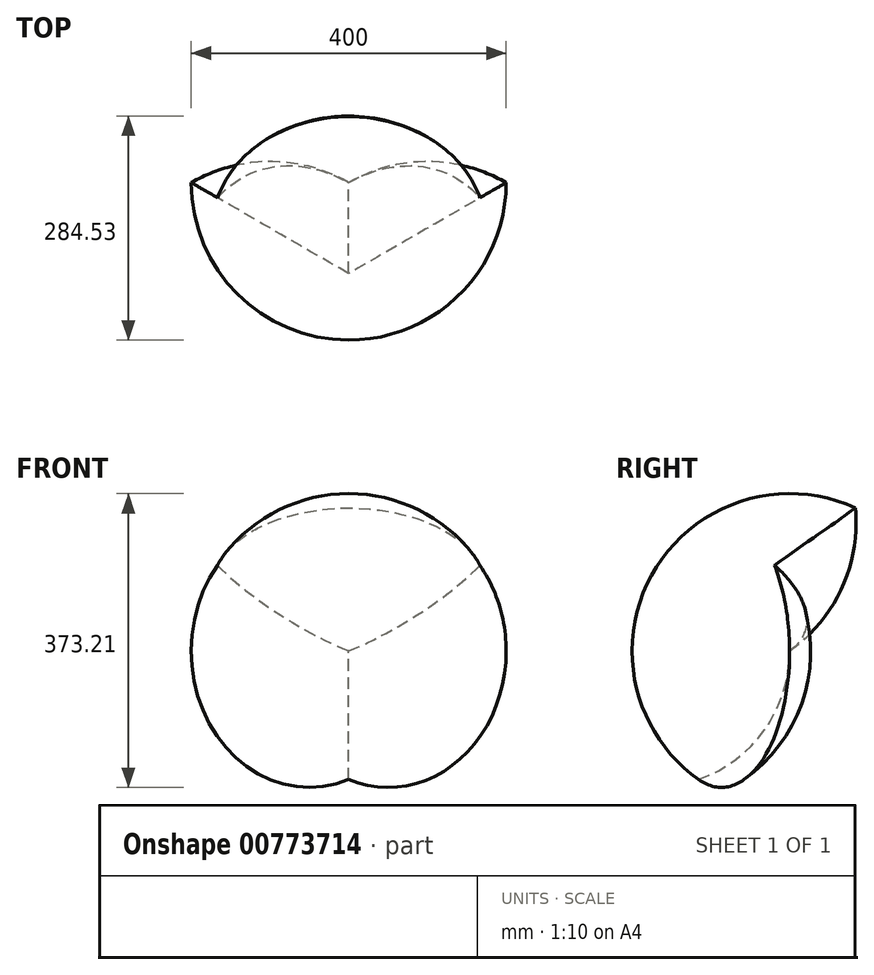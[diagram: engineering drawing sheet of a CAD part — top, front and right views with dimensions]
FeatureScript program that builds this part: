
annotation { "Feature Type Name" : "Feature", "Feature Type Description" : "" }
export const myFeature = defineFeature(function(context is Context, id is Id, definition is map)
    precondition{}
    {
        {
            var Q0;
            Q0=qCreatedBy(makeId("Top.planeOp"),FACE);
            var sketch = newSketch(context, id + "F0", { "sketchPlane" : qUnion([Q0])});
            skLineSegment(sketch, "E0", {"start": v(0, 115.47) * mm, "end": v(100, -57.74) * mm});
            skLineSegment(sketch, "E1", {"start": v(100, -57.74) * mm, "end": v(-100, -57.74) * mm});
            skLineSegment(sketch, "E2", {"start": v(-100, -57.74) * mm, "end": v(0, 115.47) * mm});
            skLineSegment(sketch, "E3", {"start": v(0, 115.47) * mm, "end": v(0, 0) * mm});
            skLineSegment(sketch, "E4", {"start": v(-100, -57.74) * mm, "end": v(0, 0) * mm});
            skLineSegment(sketch, "E5", {"start": v(0, 0) * mm, "end": v(100, -57.74) * mm});
            skPoint(sketch, "E6.orphan", {"position": v(0, -57.74) * mm});
            skLineSegment(sketch, "E7", {"start": v(0, 115.47) * mm, "end": v(0, -57.74) * mm, "construction": true});
            skCircle(sketch, "E8", {"center": v(0, 115.47) * mm, "radius": 200 * mm});
            skCircle(sketch, "E9", {"center": v(-100, -57.74) * mm, "radius": 200 * mm});
            skCircle(sketch, "E10", {"center": v(100, -57.74) * mm, "radius": 200 * mm});
            skLineSegment(sketch, "E11", {"start": v(-50, 28.87) * mm, "end": v(100, -57.74) * mm});
            skLineSegment(sketch, "E12", {"start": v(0, 115.47) * mm, "end": v(0, -57.74) * mm});
            skLineSegment(sketch, "E13", {"start": v(0, 115.47) * mm, "end": v(0, -84.53) * mm});
            skLineSegment(sketch, "E14", {"start": v(0, -84.53) * mm, "end": v(0, 315.47) * mm});
            skLineSegment(sketch, "E15", {"start": v(0, 315.47) * mm, "end": v(0, 115.47) * mm});
            skLineSegment(sketch, "E16", {"start": v(100, -57.74) * mm, "end": v(273.2, -157.74) * mm});
            skLineSegment(sketch, "E17", {"start": v(273.2, -157.74) * mm, "end": v(-73.2, 42.26) * mm});
            skLineSegment(sketch, "E18", {"start": v(-73.2, 42.26) * mm, "end": v(100, -57.74) * mm});
            skLineSegment(sketch, "E19", {"start": v(0, 0) * mm, "end": v(-273.2, -157.74) * mm});
            skLineSegment(sketch, "E20", {"start": v(-273.2, -157.74) * mm, "end": v(73.2, 42.26) * mm});
            skLineSegment(sketch, "E21", {"start": v(73.2, 42.26) * mm, "end": v(0, 0) * mm});
            skSolve(sketch);
        }
        {
            assignVariable(context, id + "F1", {"name" : "Angle", "anyValue" : 70.53});
        }
        {
            var Q0;
            {var subQ1=sQuery(id+"F0.wireOp",EDGE,"E3");var subQ6=sQuery(id+"F0.wireOp",EDGE,"E4");Q0=qUnion([makeQuery(id+"F0.imprint","IMPRINT",FACE,{"disambiguationData":[TD([[makeQuery(id+"F0.imprint","IMPRINT",EDGE,{"derivedFrom":subQ6}),1.0]])]}),makeQuery(id+"F0.imprint","IMPRINT",FACE,{"disambiguationData":[TD([[makeQuery(id+"F0.imprint","IMPRINT",EDGE,{"derivedFrom":subQ1}),-1.0]])]})]);}
            var Q1;
            {var subQ1=sQuery(id+"F0.wireOp",EDGE,"E5");var subQ5=sQuery(id+"F0.wireOp",EDGE,"E3");Q1=qUnion([makeQuery(id+"F0.imprint","IMPRINT",FACE,{"disambiguationData":[TD([[makeQuery(id+"F0.imprint","IMPRINT",EDGE,{"derivedFrom":subQ5}),1.0]])]}),makeQuery(id+"F0.imprint","IMPRINT",FACE,{"disambiguationData":[TD([[makeQuery(id+"F0.imprint","IMPRINT",EDGE,{"derivedFrom":subQ1}),1.0]])]})]);}
            var Q2;
            {var subQ1=sQuery(id+"F0.wireOp",EDGE,"E5");var subQ6=sQuery(id+"F0.wireOp",EDGE,"E4");Q2=qUnion([makeQuery(id+"F0.imprint","IMPRINT",FACE,{"disambiguationData":[TD([[makeQuery(id+"F0.imprint","IMPRINT",EDGE,{"derivedFrom":subQ6}),-1.0]])]}),makeQuery(id+"F0.imprint","IMPRINT",FACE,{"disambiguationData":[TD([[makeQuery(id+"F0.imprint","IMPRINT",EDGE,{"derivedFrom":subQ1}),-1.0]])]})]);}
            extrude(context, id + "F2", {"entities" : qUnion([Q0, Q1, Q2]), "depth" : 1000 * mm, "hasDraft" : true, "draftAngle" : (90 - getVariable(context, 'Angle')) * degree, "draftPullDirection" : true, "offsetDistance" : 25 * mm});
        }
        {
            var Q0;
            Q0=qCreatedBy(makeId("Top.planeOp"),FACE);
            cPlane(context, id + "F3", {"entities" : qUnion([Q0]), "cplaneType" : CPlaneType.OFFSET, "offset" : 163.3 * mm, "width" : 150 * mm, "height" : 150 * mm});
        }
        {
            var Q0;
            Q0=qCreatedBy(id+"F3.planeOp",FACE);
            var sketch = newSketch(context, id + "F4", { "sketchPlane" : qUnion([Q0])});
            skCircle(sketch, "E22", {"center": v(0, 0) * mm, "radius": 200 * mm});
            skLineSegment(sketch, "E23", {"start": v(0, 0) * mm, "end": v(0, 200) * mm});
            skLineSegment(sketch, "E24", {"start": v(0, 200) * mm, "end": v(0, -200) * mm});
            skLineSegment(sketch, "E25", {"start": v(0, -200) * mm, "end": v(0, 0) * mm});
            skSolve(sketch);
        }
        {
            var Q0;
            {var subQ0=sQuery(id+"F4.wireOp",EDGE,"E24");Q0=makeQuery(id+"F4.imprint","IMPRINT",FACE,{"disambiguationData":[TD([[makeQuery(id+"F4.imprint","IMPRINT",EDGE,{"derivedFrom":subQ0}),1.0]])]});}
            var Q1;
            Q1=sQuery(id+"F4.wireOp",EDGE,"E24");
            revolve(context, id + "F5", {"surfaceOperationType" : NewSurfaceOperationType.NEW, "entities" : qUnion([Q0]), "axis" : qUnion([Q1]), "revolveType" : RevolveType.FULL});
        }
        {
            var Q0;
            {var subQ0=sQuery(id+"F0.wireOp",EDGE,"E19");Q0=makeQuery(id+"F0.imprint","IMPRINT",FACE,{"disambiguationData":[TD([[makeQuery(id+"F0.imprint","IMPRINT",EDGE,{"derivedFrom":subQ0}),1.0]])]});}
            var Q1;
            {var subQ1=sQuery(id+"F0.wireOp",EDGE,"E8");var subQ4=makeQuery(id+"F0.imprint","INTERSECT",VERTEX,{"derivedFrom":[subQ1,sQuery(id+"F0.wireOp",EDGE,"E13")]});Q1=makeQuery(id+"F0.imprint","IMPRINT",FACE,{"disambiguationData":[TD([[makeQuery(id+"F0.imprint","IMPRINT",EDGE,{"disambiguationData":[TD([[subQ4,1.0]])],"derivedFrom":subQ1}),-1.0]])]});}
            var Q2;
            {var subQ3=sQuery(id+"F0.wireOp",EDGE,"E13");Q2=makeQuery(id+"F0.imprint","IMPRINT",FACE,{"disambiguationData":[TD([[makeQuery(id+"F0.imprint","IMPRINT",EDGE,{"derivedFrom":subQ3}),1.0]])]});}
            var Q3;
            {var subQ0=sQuery(id+"F0.wireOp",EDGE,"E13");Q3=makeQuery(id+"F0.imprint","IMPRINT",FACE,{"disambiguationData":[TD([[makeQuery(id+"F0.imprint","IMPRINT",EDGE,{"derivedFrom":subQ0}),-1.0]])]});}
            var Q4;
            {var subQ2=sQuery(id+"F0.wireOp",EDGE,"E4");Q4=makeQuery(id+"F0.imprint","IMPRINT",FACE,{"disambiguationData":[TD([[makeQuery(id+"F0.imprint","IMPRINT",EDGE,{"derivedFrom":subQ2}),-1.0]])]});}
            var Q5;
            {var subQ0=sQuery(id+"F0.wireOp",EDGE,"E5");Q5=makeQuery(id+"F0.imprint","IMPRINT",FACE,{"disambiguationData":[TD([[makeQuery(id+"F0.imprint","IMPRINT",EDGE,{"derivedFrom":subQ0}),-1.0]])]});}
            var Q6;
            {var subQ0=sQuery(id+"F0.wireOp",EDGE,"E9");var subQ3=sQuery(id+"F0.wireOp",EDGE,"E20");var subQ5=makeQuery(id+"F0.imprint","INTERSECT",VERTEX,{"derivedFrom":[subQ0,subQ3]});Q6=makeQuery(id+"F0.imprint","IMPRINT",FACE,{"disambiguationData":[TD([[makeQuery(id+"F0.imprint","IMPRINT",EDGE,{"disambiguationData":[TD([[subQ5,1.0]])],"derivedFrom":subQ3}),-1.0]])]});}
            var Q7;
            {var subQ0=sQuery(id+"F0.wireOp",EDGE,"E5");Q7=makeQuery(id+"F0.imprint","IMPRINT",FACE,{"disambiguationData":[TD([[makeQuery(id+"F0.imprint","IMPRINT",EDGE,{"derivedFrom":subQ0}),1.0]])]});}
            var Q8;
            Q8=sQuery(id+"F0.wireOp",EDGE,"E19");
            revolve(context, id + "F6", {"surfaceOperationType" : NewSurfaceOperationType.NEW, "entities" : qUnion([Q0, Q1, Q2, Q3, Q4, Q5, Q6, Q7]), "axis" : qUnion([Q8]), "revolveType" : RevolveType.FULL});
        }
        {
            var Q0;
            {var subQ0=sQuery(id+"F0.wireOp",EDGE,"E16");Q0=makeQuery(id+"F0.imprint","IMPRINT",FACE,{"disambiguationData":[TD([[makeQuery(id+"F0.imprint","IMPRINT",EDGE,{"derivedFrom":subQ0}),-1.0]])]});}
            var Q1;
            {var subQ1=sQuery(id+"F0.wireOp",EDGE,"E8");var subQ4=makeQuery(id+"F0.imprint","INTERSECT",VERTEX,{"derivedFrom":[subQ1,sQuery(id+"F0.wireOp",EDGE,"E13")]});Q1=makeQuery(id+"F0.imprint","IMPRINT",FACE,{"disambiguationData":[TD([[makeQuery(id+"F0.imprint","IMPRINT",EDGE,{"disambiguationData":[TD([[subQ4,1.0]])],"derivedFrom":subQ1}),-1.0]])]});}
            var Q2;
            {var subQ3=sQuery(id+"F0.wireOp",EDGE,"E13");Q2=makeQuery(id+"F0.imprint","IMPRINT",FACE,{"disambiguationData":[TD([[makeQuery(id+"F0.imprint","IMPRINT",EDGE,{"derivedFrom":subQ3}),1.0]])]});}
            var Q3;
            {var subQ0=sQuery(id+"F0.wireOp",EDGE,"E13");Q3=makeQuery(id+"F0.imprint","IMPRINT",FACE,{"disambiguationData":[TD([[makeQuery(id+"F0.imprint","IMPRINT",EDGE,{"derivedFrom":subQ0}),-1.0]])]});}
            var Q4;
            {var subQ2=sQuery(id+"F0.wireOp",EDGE,"E4");Q4=makeQuery(id+"F0.imprint","IMPRINT",FACE,{"disambiguationData":[TD([[makeQuery(id+"F0.imprint","IMPRINT",EDGE,{"derivedFrom":subQ2}),-1.0]])]});}
            var Q5;
            {var subQ0=sQuery(id+"F0.wireOp",EDGE,"E4");Q5=makeQuery(id+"F0.imprint","IMPRINT",FACE,{"disambiguationData":[TD([[makeQuery(id+"F0.imprint","IMPRINT",EDGE,{"derivedFrom":subQ0}),1.0]])]});}
            var Q6;
            {var subQ3=sQuery(id+"F0.wireOp",EDGE,"E17");Q6=makeQuery(id+"F0.imprint","IMPRINT",FACE,{"disambiguationData":[TD([[makeQuery(id+"F0.imprint","IMPRINT",EDGE,{"derivedFrom":subQ3}),1.0]])]});}
            var Q7;
            {var subQ0=sQuery(id+"F0.wireOp",EDGE,"E5");Q7=makeQuery(id+"F0.imprint","IMPRINT",FACE,{"disambiguationData":[TD([[makeQuery(id+"F0.imprint","IMPRINT",EDGE,{"derivedFrom":subQ0}),-1.0]])]});}
            var Q8;
            Q8=sQuery(id+"F0.wireOp",EDGE,"E17");
            revolve(context, id + "F7", {"operationType" : NewBodyOperationType.ADD, "surfaceOperationType" : NewSurfaceOperationType.NEW, "entities" : qUnion([Q0, Q1, Q2, Q3, Q4, Q5, Q6, Q7]), "axis" : qUnion([Q8]), "revolveType" : RevolveType.FULL});
        }
        {
            var Q0;
            {var subQ3=sQuery(id+"F0.wireOp",EDGE,"E13");Q0=makeQuery(id+"F0.imprint","IMPRINT",FACE,{"disambiguationData":[TD([[makeQuery(id+"F0.imprint","IMPRINT",EDGE,{"derivedFrom":subQ3}),1.0]])]});}
            var Q1;
            {var subQ0=sQuery(id+"F0.wireOp",EDGE,"E5");Q1=makeQuery(id+"F0.imprint","IMPRINT",FACE,{"disambiguationData":[TD([[makeQuery(id+"F0.imprint","IMPRINT",EDGE,{"derivedFrom":subQ0}),-1.0]])]});}
            var Q2;
            {var subQ0=sQuery(id+"F0.wireOp",EDGE,"E5");Q2=makeQuery(id+"F0.imprint","IMPRINT",FACE,{"disambiguationData":[TD([[makeQuery(id+"F0.imprint","IMPRINT",EDGE,{"derivedFrom":subQ0}),1.0]])]});}
            var Q3;
            {var subQ0=sQuery(id+"F0.wireOp",EDGE,"E9");var subQ3=sQuery(id+"F0.wireOp",EDGE,"E20");var subQ5=makeQuery(id+"F0.imprint","INTERSECT",VERTEX,{"derivedFrom":[subQ0,subQ3]});Q3=makeQuery(id+"F0.imprint","IMPRINT",FACE,{"disambiguationData":[TD([[makeQuery(id+"F0.imprint","IMPRINT",EDGE,{"disambiguationData":[TD([[subQ5,1.0]])],"derivedFrom":subQ3}),-1.0]])]});}
            var Q4;
            {var subQ0=sQuery(id+"F0.wireOp",EDGE,"E9");var subQ3=sQuery(id+"F0.wireOp",EDGE,"E20");var subQ5=makeQuery(id+"F0.imprint","INTERSECT",VERTEX,{"derivedFrom":[subQ0,subQ3]});Q4=makeQuery(id+"F0.imprint","IMPRINT",FACE,{"disambiguationData":[TD([[makeQuery(id+"F0.imprint","IMPRINT",EDGE,{"disambiguationData":[TD([[subQ5,1.0]])],"derivedFrom":subQ3}),1.0]])]});}
            var Q5;
            {var subQ0=sQuery(id+"F0.wireOp",EDGE,"E3");Q5=makeQuery(id+"F0.imprint","IMPRINT",FACE,{"disambiguationData":[TD([[makeQuery(id+"F0.imprint","IMPRINT",EDGE,{"derivedFrom":subQ0}),1.0]])]});}
            var Q6;
            {var subQ1=sQuery(id+"F0.wireOp",EDGE,"E8");var subQ4=sQuery(id+"F0.wireOp",EDGE,"E10");var subQ5=makeQuery(id+"F0.imprint","INTERSECT",VERTEX,{"derivedFrom":[subQ1,subQ4]});Q6=makeQuery(id+"F0.imprint","IMPRINT",FACE,{"disambiguationData":[TD([[makeQuery(id+"F0.imprint","IMPRINT",EDGE,{"disambiguationData":[TD([[subQ5,1.0]])],"derivedFrom":subQ1}),1.0]])]});}
            var Q7;
            {var subQ0=sQuery(id+"F0.wireOp",EDGE,"E14");Q7=makeQuery(id+"F0.imprint","IMPRINT",FACE,{"disambiguationData":[TD([[makeQuery(id+"F0.imprint","IMPRINT",EDGE,{"derivedFrom":subQ0}),-1.0]])]});}
            var Q8;
            Q8=sQuery(id+"F0.wireOp",EDGE,"E15");
            revolve(context, id + "F8", {"surfaceOperationType" : NewSurfaceOperationType.NEW, "entities" : qUnion([Q0, Q1, Q2, Q3, Q4, Q5, Q6, Q7]), "axis" : qUnion([Q8]), "revolveType" : RevolveType.FULL});
        }
        {
            var Q0;
            Q0=makeQuery(id+"F2.opExtrude","SWEPT_BODY",BODY,{"disambiguationData":[OSD([sQuery(id+"F0.wireOp",EDGE,"E0"),sQuery(id+"F0.wireOp",EDGE,"E1"),sQuery(id+"F0.wireOp",EDGE,"E2")])]});
            var Q1;
            Q1=makeQuery(id+"F6.opRevolve","SWEPT_BODY",BODY,{"disambiguationData":[OSD([sQuery(id+"F0.wireOp",EDGE,"E4"),sQuery(id+"F0.wireOp",EDGE,"E9"),sQuery(id+"F0.wireOp",EDGE,"E19"),sQuery(id+"F0.wireOp",EDGE,"E20")])]});
            var Q2;
            Q2=makeQuery(id+"F8.opRevolve","SWEPT_BODY",BODY,{"disambiguationData":[OSD([sQuery(id+"F0.wireOp",EDGE,"E3"),sQuery(id+"F0.wireOp",EDGE,"E8"),sQuery(id+"F0.wireOp",EDGE,"E12"),sQuery(id+"F0.wireOp",EDGE,"E13"),sQuery(id+"F0.wireOp",EDGE,"E14")])]});
            var Q3;
            Q3=makeQuery(id+"F5.opRevolve","SWEPT_BODY",BODY,{"disambiguationData":[OSD([sQuery(id+"F4.wireOp",EDGE,"E22"),sQuery(id+"F4.wireOp",EDGE,"E24"),sQuery(id+"F4.wireOp",EDGE,"E25")])]});
            booleanBodies(context, id + "F9", {"operationType" : BooleanOperationType.INTERSECTION, "tools" : qUnion([Q0, Q1, Q2, Q3])});
        }
    });
